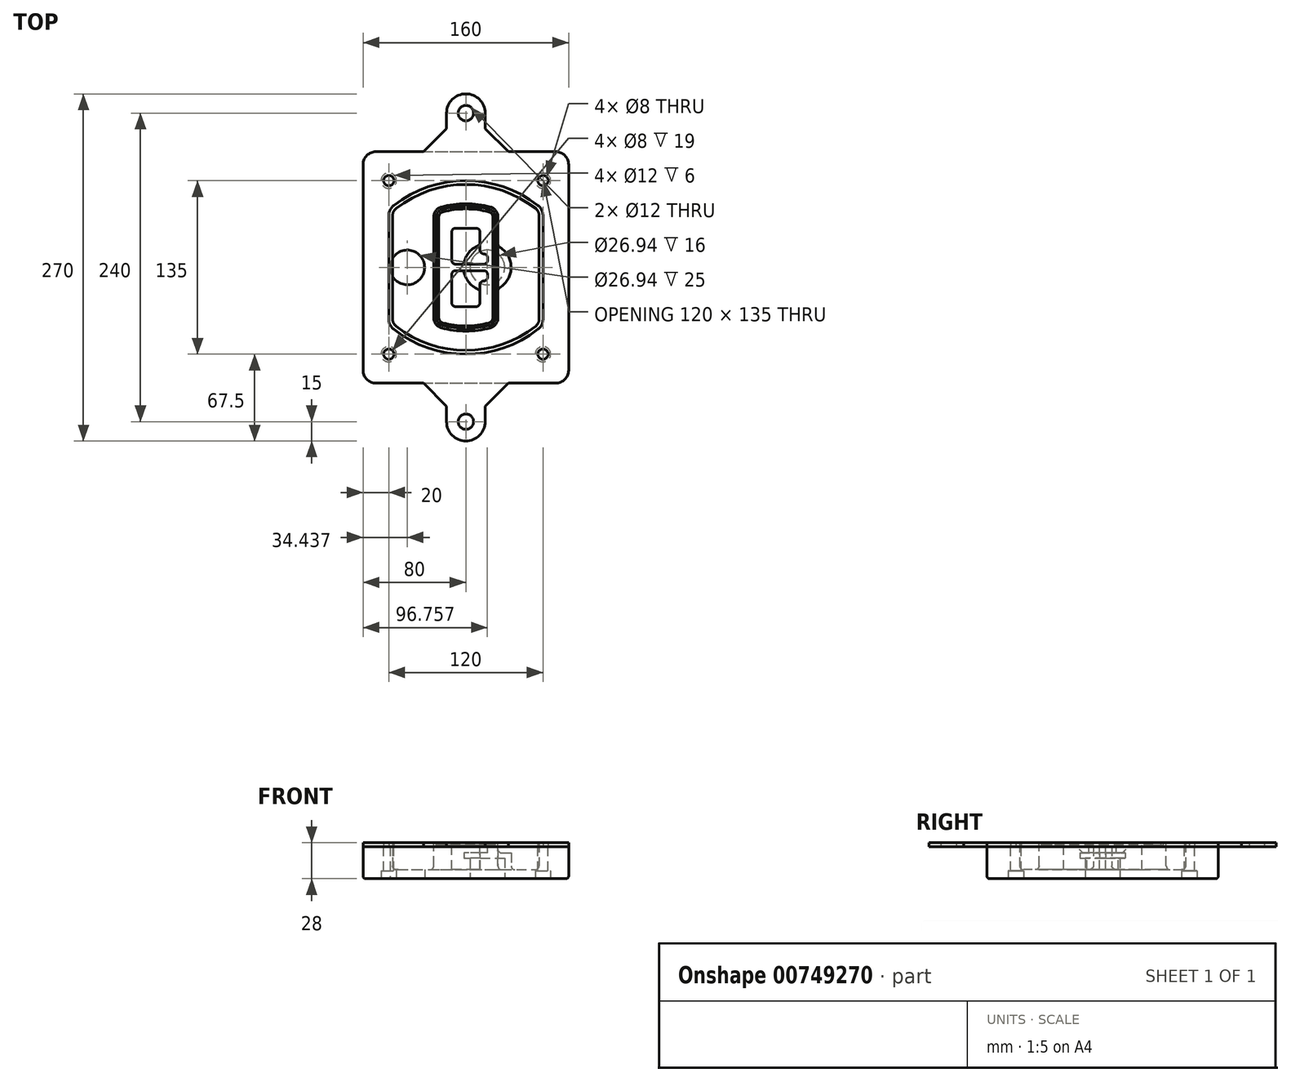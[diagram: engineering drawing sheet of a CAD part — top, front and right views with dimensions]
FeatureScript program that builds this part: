
annotation { "Feature Type Name" : "Feature", "Feature Type Description" : "" }
export const myFeature = defineFeature(function(context is Context, id is Id, definition is map)
    precondition{}
    {
        {
            var Q0;
            Q0=qCreatedBy(makeId("Top.planeOp"),FACE);
            var sketch = newSketch(context, id + "F0", { "sketchPlane" : qUnion([Q0])});
            skPoint(sketch, "E0.rect.middle", {"position": v(0, 0) * mm});
            skLineSegment(sketch, "E1.bottom", {"start": v(-70, -90) * mm, "end": v(70, -90) * mm});
            skLineSegment(sketch, "E1.top", {"start": v(-70, 90) * mm, "end": v(70, 90) * mm});
            skLineSegment(sketch, "E1.left", {"start": v(-80, -80) * mm, "end": v(-80, 80) * mm});
            skLineSegment(sketch, "E1.right", {"start": v(80, -80) * mm, "end": v(80, 80) * mm});
            skLineSegment(sketch, "E2", {"start": v(-80, 90) * mm, "end": v(80, -90) * mm, "construction": true});
            skLineSegment(sketch, "E3", {"start": v(80, 90) * mm, "end": v(-80, -90) * mm, "construction": true});
            skCircle(sketch, "E4", {"center": v(-60, 67.5) * mm, "radius": 4 * mm});
            skCircle(sketch, "E5", {"center": v(60, 67.5) * mm, "radius": 4 * mm});
            skCircle(sketch, "E6", {"center": v(60, -67.5) * mm, "radius": 4 * mm});
            skCircle(sketch, "E7", {"center": v(-60, -67.5) * mm, "radius": 4 * mm});
            skLineSegment(sketch, "E8", {"start": v(-60, 67.5) * mm, "end": v(60, 67.5) * mm, "construction": true});
            skLineSegment(sketch, "E9", {"start": v(60, 67.5) * mm, "end": v(60, -67.5) * mm, "construction": true});
            skLineSegment(sketch, "E10", {"start": v(60, -67.5) * mm, "end": v(-60, -67.5) * mm, "construction": true});
            skLineSegment(sketch, "E11", {"start": v(-60, -67.5) * mm, "end": v(-60, 67.5) * mm, "construction": true});
            skLineSegment(sketch, "E12", {"start": v(-60, 40.3) * mm, "end": v(-60, -40.3) * mm});
            skLineSegment(sketch, "E13", {"start": v(60, 40.3) * mm, "end": v(60, -40.3) * mm});
            skArc(sketch, "E14", {"start": v(56.15, 48.18) * mm, "mid": v(0, 67.5) * mm, "end": v(-56.15, 48.18) * mm});
            skArc(sketch, "E15", {"start": v(-56.15, -48.18) * mm, "mid": v(0, -67.5) * mm, "end": v(56.15, -48.18) * mm});
            skLineSegment(sketch, "E16", {"start": v(-60, 0) * mm, "end": v(60, 0) * mm, "construction": true});
            skPoint(sketch, "E17.visualSharp", {"position": v(-60, -45) * mm});
            skArc(sketch, "E17.filletArc", {"start": v(-60, -40.3) * mm, "mid": v(-58.99, -44.68) * mm, "end": v(-56.15, -48.18) * mm});
            skPoint(sketch, "E18.visualSharp", {"position": v(-60, 45) * mm});
            skArc(sketch, "E18.filletArc", {"start": v(-56.15, 48.18) * mm, "mid": v(-58.99, 44.68) * mm, "end": v(-60, 40.3) * mm});
            skPoint(sketch, "E19.visualSharp", {"position": v(60, 45) * mm});
            skArc(sketch, "E19.filletArc", {"start": v(60, 40.3) * mm, "mid": v(58.99, 44.68) * mm, "end": v(56.15, 48.18) * mm});
            skPoint(sketch, "E20.visualSharp", {"position": v(60, -45) * mm});
            skArc(sketch, "E20.filletArc", {"start": v(56.15, -48.18) * mm, "mid": v(58.99, -44.68) * mm, "end": v(60, -40.3) * mm});
            skPoint(sketch, "E21.visualSharp", {"position": v(-80, 90) * mm});
            skArc(sketch, "E21.filletArc", {"start": v(-70, 90) * mm, "mid": v(-77.07, 87.07) * mm, "end": v(-80, 80) * mm});
            skPoint(sketch, "E22.visualSharp", {"position": v(80, 90) * mm});
            skArc(sketch, "E22.filletArc", {"start": v(80, 80) * mm, "mid": v(77.07, 87.07) * mm, "end": v(70, 90) * mm});
            skPoint(sketch, "E23.visualSharp", {"position": v(80, -90) * mm});
            skArc(sketch, "E23.filletArc", {"start": v(70, -90) * mm, "mid": v(77.07, -87.07) * mm, "end": v(80, -80) * mm});
            skPoint(sketch, "E24.visualSharp", {"position": v(-80, -90) * mm});
            skArc(sketch, "E24.filletArc", {"start": v(-80, -80) * mm, "mid": v(-77.07, -87.07) * mm, "end": v(-70, -90) * mm});
            skArc(sketch, "E25.0", {"start": v(57, 40.3) * mm, "mid": v(56.3, 43.36) * mm, "end": v(54.3, 45.81) * mm});
            skLineSegment(sketch, "E25.1", {"start": v(57, 40.3) * mm, "end": v(57, -40.3) * mm});
            skArc(sketch, "E25.2", {"start": v(54.3, -45.81) * mm, "mid": v(56.3, -43.36) * mm, "end": v(57, -40.3) * mm});
            skArc(sketch, "E25.3", {"start": v(-54.3, -45.81) * mm, "mid": v(0, -64.5) * mm, "end": v(54.3, -45.81) * mm});
            skArc(sketch, "E25.4", {"start": v(-57, -40.3) * mm, "mid": v(-56.3, -43.36) * mm, "end": v(-54.3, -45.81) * mm});
            skArc(sketch, "E25.5", {"start": v(54.3, 45.81) * mm, "mid": v(0, 64.5) * mm, "end": v(-54.3, 45.81) * mm});
            skLineSegment(sketch, "E25.6", {"start": v(-57, 40.3) * mm, "end": v(-57, -40.3) * mm});
            skArc(sketch, "E25.7", {"start": v(-54.3, 45.81) * mm, "mid": v(-56.3, 43.36) * mm, "end": v(-57, 40.3) * mm});
            skArc(sketch, "E26.0", {"start": v(-58.62, 51.33) * mm, "mid": v(-62.58, 46.43) * mm, "end": v(-64, 40.3) * mm});
            skArc(sketch, "E26.1", {"start": v(58.62, 51.33) * mm, "mid": v(0, 71.5) * mm, "end": v(-58.62, 51.33) * mm});
            skArc(sketch, "E26.2", {"start": v(64, 40.3) * mm, "mid": v(62.58, 46.43) * mm, "end": v(58.62, 51.33) * mm});
            skLineSegment(sketch, "E26.3", {"start": v(64, 40.3) * mm, "end": v(64, -40.3) * mm});
            skArc(sketch, "E26.4", {"start": v(58.62, -51.33) * mm, "mid": v(62.58, -46.43) * mm, "end": v(64, -40.3) * mm});
            skLineSegment(sketch, "E26.5", {"start": v(-64, 40.3) * mm, "end": v(-64, -40.3) * mm});
            skArc(sketch, "E26.6", {"start": v(-58.62, -51.33) * mm, "mid": v(0, -71.5) * mm, "end": v(58.62, -51.33) * mm});
            skArc(sketch, "E26.7", {"start": v(-64, -40.3) * mm, "mid": v(-62.58, -46.43) * mm, "end": v(-58.62, -51.33) * mm});
            skSolve(sketch);
        }
        {
            var Q0;
            Q0=makeQuery(id+"F0.imprint","IMPRINT",FACE,{"disambiguationData":[TD([[makeQuery(id+"F0.imprint","IMPRINT",EDGE,{"derivedFrom":sQuery(id+"F0.wireOp",EDGE,"E1.bottom")}),1.0]])]});
            var Q1;
            Q1=makeQuery(id+"F0.imprint","IMPRINT",FACE,{"disambiguationData":[TD([[makeQuery(id+"F0.imprint","IMPRINT",EDGE,{"derivedFrom":sQuery(id+"F0.wireOp",EDGE,"E12")}),1.0]])]});
            var Q2;
            Q2=makeQuery(id+"F0.imprint","IMPRINT",FACE,{"disambiguationData":[TD([[makeQuery(id+"F0.imprint","IMPRINT",EDGE,{"derivedFrom":sQuery(id+"F0.wireOp",EDGE,"E25.0")}),1.0]])]});
            var Q3;
            Q3=makeQuery(id+"F0.imprint","IMPRINT",FACE,{"disambiguationData":[TD([[makeQuery(id+"F0.imprint","IMPRINT",EDGE,{"derivedFrom":sQuery(id+"F0.wireOp",EDGE,"E12")}),-1.0]])]});
            extrude(context, id + "F1", {"entities" : qUnion([Q0, Q1, Q2, Q3]), "oppositeDirection" : true, "depth" : 25 * mm});
        }
        {
            var Q0;
            Q0=makeQuery(id+"F0.imprint","IMPRINT",FACE,{"disambiguationData":[TD([[makeQuery(id+"F0.imprint","IMPRINT",EDGE,{"derivedFrom":sQuery(id+"F0.wireOp",EDGE,"E12")}),1.0]])]});
            extrude(context, id + "F2", {"entities" : qUnion([Q0]), "operationType" : NewBodyOperationType.ADD, "depth" : 3 * mm});
        }
        {
            var Q0;
            Q0=makeQuery(id+"F0.imprint","IMPRINT",FACE,{"disambiguationData":[TD([[makeQuery(id+"F0.imprint","IMPRINT",EDGE,{"derivedFrom":sQuery(id+"F0.wireOp",EDGE,"E25.0")}),1.0]])]});
            extrude(context, id + "F3", {"entities" : qUnion([Q0]), "operationType" : NewBodyOperationType.REMOVE, "oppositeDirection" : true, "depth" : 18 * mm});
        }
        {
            var Q0;
            Q0=makeQuery(id+"F2.opExtrude","CAP_FACE",FACE,{"disambiguationData":[OSD([sQuery(id+"F0.wireOp",EDGE,"E12"),sQuery(id+"F0.wireOp",EDGE,"E13"),sQuery(id+"F0.wireOp",EDGE,"E14"),sQuery(id+"F0.wireOp",EDGE,"E15"),sQuery(id+"F0.wireOp",EDGE,"E17.filletArc"),sQuery(id+"F0.wireOp",EDGE,"E18.filletArc"),sQuery(id+"F0.wireOp",EDGE,"E19.filletArc"),sQuery(id+"F0.wireOp",EDGE,"E20.filletArc"),sQuery(id+"F0.wireOp",EDGE,"E25.0"),sQuery(id+"F0.wireOp",EDGE,"E25.1"),sQuery(id+"F0.wireOp",EDGE,"E25.2"),sQuery(id+"F0.wireOp",EDGE,"E25.3"),sQuery(id+"F0.wireOp",EDGE,"E25.4"),sQuery(id+"F0.wireOp",EDGE,"E25.5"),sQuery(id+"F0.wireOp",EDGE,"E25.6"),sQuery(id+"F0.wireOp",EDGE,"E25.7")])],"isStart":false});
            var sketch = newSketch(context, id + "F4", { "sketchPlane" : qUnion([Q0])});
            skArc(sketch, "E27.0", {"start": v(-19.08, -46.97) * mm, "mid": v(0, -49.5) * mm, "end": v(19.08, -46.97) * mm});
            skArc(sketch, "E28.0", {"start": v(19.08, 46.97) * mm, "mid": v(0, 49.5) * mm, "end": v(-19.08, 46.97) * mm});
            skLineSegment(sketch, "E29", {"start": v(-25, 39.25) * mm, "end": v(-25, -39.25) * mm});
            skLineSegment(sketch, "E30", {"start": v(25, 39.25) * mm, "end": v(25, -39.25) * mm});
            skLineSegment(sketch, "E31", {"start": v(-25, 45.1) * mm, "end": v(25, 45.1) * mm, "construction": true});
            skLineSegment(sketch, "E32", {"start": v(-25, -45.1) * mm, "end": v(25, -45.1) * mm, "construction": true});
            skPoint(sketch, "E33.visualSharp", {"position": v(-25, 45.1) * mm});
            skArc(sketch, "E33.filletArc", {"start": v(-19.08, 46.97) * mm, "mid": v(-23.35, 44.11) * mm, "end": v(-25, 39.25) * mm});
            skPoint(sketch, "E34.visualSharp", {"position": v(25, 45.1) * mm});
            skArc(sketch, "E34.filletArc", {"start": v(25, 39.25) * mm, "mid": v(23.35, 44.11) * mm, "end": v(19.08, 46.97) * mm});
            skPoint(sketch, "E35.visualSharp", {"position": v(25, -45.1) * mm});
            skArc(sketch, "E35.filletArc", {"start": v(19.08, -46.97) * mm, "mid": v(23.35, -44.11) * mm, "end": v(25, -39.25) * mm});
            skPoint(sketch, "E36.visualSharp", {"position": v(-25, -45.1) * mm});
            skArc(sketch, "E36.filletArc", {"start": v(-25, -39.25) * mm, "mid": v(-23.35, -44.11) * mm, "end": v(-19.08, -46.97) * mm});
            skArc(sketch, "E37.0", {"start": v(54.3, 45.81) * mm, "mid": v(0, 64.5) * mm, "end": v(-54.3, 45.81) * mm});
            skArc(sketch, "E37.1", {"start": v(-54.3, 45.81) * mm, "mid": v(-56.3, 43.36) * mm, "end": v(-57, 40.3) * mm});
            skLineSegment(sketch, "E37.2", {"start": v(-57, 40.3) * mm, "end": v(-57, -40.3) * mm});
            skArc(sketch, "E37.3", {"start": v(-57, -40.3) * mm, "mid": v(-56.3, -43.36) * mm, "end": v(-54.3, -45.81) * mm});
            skArc(sketch, "E37.4", {"start": v(-54.3, -45.81) * mm, "mid": v(0, -64.5) * mm, "end": v(54.3, -45.81) * mm});
            skArc(sketch, "E37.5", {"start": v(54.3, -45.81) * mm, "mid": v(56.3, -43.36) * mm, "end": v(57, -40.3) * mm});
            skLineSegment(sketch, "E37.6", {"start": v(57, 40.3) * mm, "end": v(57, -40.3) * mm});
            skArc(sketch, "E37.7", {"start": v(57, 40.3) * mm, "mid": v(56.3, 43.36) * mm, "end": v(54.3, 45.81) * mm});
            skLineSegment(sketch, "E38.0", {"start": v(23, 39.25) * mm, "end": v(23, -39.25) * mm});
            skArc(sketch, "E38.1", {"start": v(18.56, -45.04) * mm, "mid": v(21.76, -42.9) * mm, "end": v(23, -39.25) * mm});
            skArc(sketch, "E38.2", {"start": v(-18.56, -45.04) * mm, "mid": v(0, -47.5) * mm, "end": v(18.56, -45.04) * mm});
            skArc(sketch, "E38.3", {"start": v(-23, -39.25) * mm, "mid": v(-21.76, -42.9) * mm, "end": v(-18.56, -45.04) * mm});
            skLineSegment(sketch, "E38.4", {"start": v(-23, 39.25) * mm, "end": v(-23, -39.25) * mm});
            skArc(sketch, "E38.5", {"start": v(23, 39.25) * mm, "mid": v(21.76, 42.9) * mm, "end": v(18.56, 45.04) * mm});
            skArc(sketch, "E38.6", {"start": v(-18.56, 45.04) * mm, "mid": v(-21.76, 42.9) * mm, "end": v(-23, 39.25) * mm});
            skArc(sketch, "E38.7", {"start": v(18.56, 45.04) * mm, "mid": v(0, 47.5) * mm, "end": v(-18.56, 45.04) * mm});
            skArc(sketch, "E39.0", {"start": v(21, 39.25) * mm, "mid": v(20.18, 41.68) * mm, "end": v(18.04, 43.1) * mm});
            skLineSegment(sketch, "E39.1", {"start": v(21, 39.25) * mm, "end": v(21, -39.25) * mm});
            skArc(sketch, "E39.2", {"start": v(18.04, -43.1) * mm, "mid": v(20.18, -41.68) * mm, "end": v(21, -39.25) * mm});
            skArc(sketch, "E39.3", {"start": v(-18.04, -43.1) * mm, "mid": v(0, -45.5) * mm, "end": v(18.04, -43.1) * mm});
            skArc(sketch, "E39.4", {"start": v(-21, -39.25) * mm, "mid": v(-20.18, -41.68) * mm, "end": v(-18.04, -43.1) * mm});
            skArc(sketch, "E39.5", {"start": v(18.04, 43.1) * mm, "mid": v(0, 45.5) * mm, "end": v(-18.04, 43.1) * mm});
            skLineSegment(sketch, "E39.6", {"start": v(-21, 39.25) * mm, "end": v(-21, -39.25) * mm});
            skArc(sketch, "E39.7", {"start": v(-18.04, 43.1) * mm, "mid": v(-20.18, 41.68) * mm, "end": v(-21, 39.25) * mm});
            skLineSegment(sketch, "E40", {"start": v(-25, 0) * mm, "end": v(25, 0) * mm, "construction": true});
            skLineSegment(sketch, "E41", {"start": v(-11, 5.5) * mm, "end": v(-11, 27.5) * mm});
            skLineSegment(sketch, "E42", {"start": v(-8, 30.5) * mm, "end": v(8, 30.5) * mm});
            skLineSegment(sketch, "E43", {"start": v(11, 27.5) * mm, "end": v(11, 13.5) * mm});
            skLineSegment(sketch, "E44", {"start": v(14, 10.5) * mm, "end": v(14, 10.5) * mm});
            skLineSegment(sketch, "E45", {"start": v(17, 7.5) * mm, "end": v(17, 5.5) * mm});
            skLineSegment(sketch, "E46", {"start": v(14, 2.5) * mm, "end": v(-8, 2.5) * mm});
            skPoint(sketch, "E47.visualSharp", {"position": v(-11, 30.5) * mm});
            skArc(sketch, "E47.filletArc", {"start": v(-8, 30.5) * mm, "mid": v(-10.12, 29.62) * mm, "end": v(-11, 27.5) * mm});
            skPoint(sketch, "E48.visualSharp", {"position": v(11, 30.5) * mm});
            skArc(sketch, "E48.filletArc", {"start": v(11, 27.5) * mm, "mid": v(10.12, 29.62) * mm, "end": v(8, 30.5) * mm});
            skPoint(sketch, "E49.visualSharp", {"position": v(11, 10.5) * mm});
            skArc(sketch, "E49.filletArc", {"start": v(11, 13.5) * mm, "mid": v(11.88, 11.38) * mm, "end": v(14, 10.5) * mm});
            skPoint(sketch, "E50.visualSharp", {"position": v(17, 10.5) * mm});
            skArc(sketch, "E50.filletArc", {"start": v(17, 7.5) * mm, "mid": v(16.12, 9.62) * mm, "end": v(14, 10.5) * mm});
            skPoint(sketch, "E51.visualSharp", {"position": v(17, 2.5) * mm});
            skArc(sketch, "E51.filletArc", {"start": v(14, 2.5) * mm, "mid": v(16.12, 3.38) * mm, "end": v(17, 5.5) * mm});
            skPoint(sketch, "E52.visualSharp", {"position": v(-11, 2.5) * mm});
            skArc(sketch, "E52.filletArc", {"start": v(-11, 5.5) * mm, "mid": v(-10.12, 3.38) * mm, "end": v(-8, 2.5) * mm});
            skLineSegment(sketch, "E53.0.MirrorCS", {"start": v(14, -2.5) * mm, "end": v(-8, -2.5) * mm});
            skArc(sketch, "E54.0.MirrorCS", {"start": v(-11, -5.5) * mm, "mid": v(-10.12, -3.38) * mm, "end": v(-8, -2.5) * mm});
            skLineSegment(sketch, "E55.0.MirrorCS", {"start": v(-11, -5.5) * mm, "end": v(-11, -27.5) * mm});
            skArc(sketch, "E56.0.MirrorCS", {"start": v(-8, -30.5) * mm, "mid": v(-10.12, -29.62) * mm, "end": v(-11, -27.5) * mm});
            skLineSegment(sketch, "E57.0.MirrorCS", {"start": v(-8, -30.5) * mm, "end": v(8, -30.5) * mm});
            skArc(sketch, "E58.0.MirrorCS", {"start": v(11, -27.5) * mm, "mid": v(10.12, -29.62) * mm, "end": v(8, -30.5) * mm});
            skLineSegment(sketch, "E59.0.MirrorCS", {"start": v(11, -27.5) * mm, "end": v(11, -13.5) * mm});
            skArc(sketch, "E60.0.MirrorCS", {"start": v(11, -13.5) * mm, "mid": v(11.88, -11.38) * mm, "end": v(14, -10.5) * mm});
            skArc(sketch, "E61.0.MirrorCS", {"start": v(17, -7.5) * mm, "mid": v(16.12, -9.62) * mm, "end": v(14, -10.5) * mm});
            skLineSegment(sketch, "E62.0.MirrorCS", {"start": v(17, -7.5) * mm, "end": v(17, -5.5) * mm});
            skArc(sketch, "E63.0.MirrorCS", {"start": v(14, -2.5) * mm, "mid": v(16.12, -3.38) * mm, "end": v(17, -5.5) * mm});
            skSolve(sketch);
        }
        {
            var Q0;
            Q0=makeQuery(id+"F4.imprint","IMPRINT",FACE,{"disambiguationData":[TD([[makeQuery(id+"F4.imprint","IMPRINT",EDGE,{"derivedFrom":sQuery(id+"F4.wireOp",EDGE,"E27.0")}),1.0]])]});
            var Q1;
            Q1=makeQuery(id+"F4.imprint","IMPRINT",FACE,{"disambiguationData":[TD([[makeQuery(id+"F4.imprint","IMPRINT",EDGE,{"derivedFrom":sQuery(id+"F4.wireOp",EDGE,"E38.0")}),-1.0]])]});
            var Q2;
            Q2=makeQuery(id+"F4.imprint","IMPRINT",FACE,{"disambiguationData":[TD([[makeQuery(id+"F4.imprint","IMPRINT",EDGE,{"derivedFrom":sQuery(id+"F4.wireOp",EDGE,"E39.0")}),1.0]])]});
            extrude(context, id + "F5", {"entities" : qUnion([Q0, Q1, Q2]), "operationType" : NewBodyOperationType.ADD, "endBound" : BoundingType.UP_TO_NEXT, "oppositeDirection" : true, "depth" : 25 * mm});
        }
        {
            var Q0;
            Q0=makeQuery(id+"F4.imprint","IMPRINT",FACE,{"disambiguationData":[TD([[makeQuery(id+"F4.imprint","IMPRINT",EDGE,{"derivedFrom":sQuery(id+"F4.wireOp",EDGE,"E38.0")}),-1.0]])]});
            extrude(context, id + "F6", {"entities" : qUnion([Q0]), "operationType" : NewBodyOperationType.REMOVE, "oppositeDirection" : true, "depth" : 2 * mm});
        }
        {
            var Q0;
            Q0=makeQuery(id+"F1.opExtrude","CAP_FACE",FACE,{"disambiguationData":[OSD([sQuery(id+"F0.wireOp",EDGE,"E1.bottom"),sQuery(id+"F0.wireOp",EDGE,"E1.top"),sQuery(id+"F0.wireOp",EDGE,"E1.left"),sQuery(id+"F0.wireOp",EDGE,"E1.right"),sQuery(id+"F0.wireOp",EDGE,"E4"),sQuery(id+"F0.wireOp",EDGE,"E5"),sQuery(id+"F0.wireOp",EDGE,"E6"),sQuery(id+"F0.wireOp",EDGE,"E7"),sQuery(id+"F0.wireOp",EDGE,"E21.filletArc"),sQuery(id+"F0.wireOp",EDGE,"E22.filletArc"),sQuery(id+"F0.wireOp",EDGE,"E23.filletArc"),sQuery(id+"F0.wireOp",EDGE,"E24.filletArc")])],"isStart":false});
            var sketch = newSketch(context, id + "F7", { "sketchPlane" : qUnion([Q0])});
            skCircle(sketch, "E64", {"center": v(16.76, 0) * mm, "radius": 13.47 * mm});
            skCircle(sketch, "E65", {"center": v(-45.56, 0) * mm, "radius": 13.47 * mm});
            skLineSegment(sketch, "E66", {"start": v(80, 0) * mm, "end": v(-80, 0) * mm});
            skCircle(sketch, "E67", {"center": v(16.76, 0) * mm, "radius": 18.47 * mm});
            skCircle(sketch, "E68", {"center": v(60, -67.5) * mm, "radius": 6 * mm});
            skCircle(sketch, "E69", {"center": v(-60, -67.5) * mm, "radius": 6 * mm});
            skCircle(sketch, "E70", {"center": v(-60, 67.5) * mm, "radius": 6 * mm});
            skCircle(sketch, "E71", {"center": v(60, 67.5) * mm, "radius": 6 * mm});
            skSolve(sketch);
        }
        {
            var Q0;
            {var subQ1=sQuery(id+"F7.wireOp",EDGE,"E66");var subQ4=sQuery(id+"F7.wireOp",EDGE,"E64");var subQ6=makeQuery(id+"F7.imprint","INTERSECT",VERTEX,{"disambiguationData":[OD(0.0)],"derivedFrom":[subQ4,subQ1]});Q0=makeQuery(id+"F7.imprint","IMPRINT",FACE,{"disambiguationData":[TD([[makeQuery(id+"F7.imprint","IMPRINT",EDGE,{"disambiguationData":[TD([[subQ6,-1.0]])],"derivedFrom":subQ4}),-1.0]])]});}
            var Q1;
            {var subQ0=sQuery(id+"F7.wireOp",EDGE,"E66");var subQ1=sQuery(id+"F7.wireOp",EDGE,"E64");var subQ3=makeQuery(id+"F7.imprint","INTERSECT",VERTEX,{"disambiguationData":[OD(0.0)],"derivedFrom":[subQ1,subQ0]});Q1=makeQuery(id+"F7.imprint","IMPRINT",FACE,{"disambiguationData":[TD([[makeQuery(id+"F7.imprint","IMPRINT",EDGE,{"disambiguationData":[TD([[subQ3,-1.0]])],"derivedFrom":subQ1}),1.0]])]});}
            var Q2;
            {var subQ0=sQuery(id+"F7.wireOp",EDGE,"E66");var subQ1=sQuery(id+"F7.wireOp",EDGE,"E64");var subQ3=makeQuery(id+"F7.imprint","INTERSECT",VERTEX,{"disambiguationData":[OD(0.0)],"derivedFrom":[subQ1,subQ0]});Q2=makeQuery(id+"F7.imprint","IMPRINT",FACE,{"disambiguationData":[TD([[makeQuery(id+"F7.imprint","IMPRINT",EDGE,{"disambiguationData":[TD([[subQ3,1.0]])],"derivedFrom":subQ1}),1.0]])]});}
            var Q3;
            {var subQ1=sQuery(id+"F7.wireOp",EDGE,"E66");var subQ4=sQuery(id+"F7.wireOp",EDGE,"E64");var subQ6=makeQuery(id+"F7.imprint","INTERSECT",VERTEX,{"disambiguationData":[OD(0.0)],"derivedFrom":[subQ4,subQ1]});Q3=makeQuery(id+"F7.imprint","IMPRINT",FACE,{"disambiguationData":[TD([[makeQuery(id+"F7.imprint","IMPRINT",EDGE,{"disambiguationData":[TD([[subQ6,1.0]])],"derivedFrom":subQ4}),-1.0]])]});}
            extrude(context, id + "F8", {"entities" : qUnion([Q0, Q1, Q2, Q3]), "operationType" : NewBodyOperationType.ADD, "oppositeDirection" : true, "depth" : 20 * mm});
        }
        {
            var Q0;
            {var subQ0=sQuery(id+"F7.wireOp",EDGE,"E66");var subQ1=sQuery(id+"F7.wireOp",EDGE,"E64");var subQ3=makeQuery(id+"F7.imprint","INTERSECT",VERTEX,{"disambiguationData":[OD(0.0)],"derivedFrom":[subQ1,subQ0]});Q0=makeQuery(id+"F7.imprint","IMPRINT",FACE,{"disambiguationData":[TD([[makeQuery(id+"F7.imprint","IMPRINT",EDGE,{"disambiguationData":[TD([[subQ3,-1.0]])],"derivedFrom":subQ1}),1.0]])]});}
            var Q1;
            {var subQ0=sQuery(id+"F7.wireOp",EDGE,"E66");var subQ1=sQuery(id+"F7.wireOp",EDGE,"E64");var subQ3=makeQuery(id+"F7.imprint","INTERSECT",VERTEX,{"disambiguationData":[OD(0.0)],"derivedFrom":[subQ1,subQ0]});Q1=makeQuery(id+"F7.imprint","IMPRINT",FACE,{"disambiguationData":[TD([[makeQuery(id+"F7.imprint","IMPRINT",EDGE,{"disambiguationData":[TD([[subQ3,1.0]])],"derivedFrom":subQ1}),1.0]])]});}
            extrude(context, id + "F9", {"entities" : qUnion([Q0, Q1]), "operationType" : NewBodyOperationType.REMOVE, "oppositeDirection" : true, "depth" : 16 * mm});
        }
        {
            var Q0;
            {var subQ0=sQuery(id+"F7.wireOp",EDGE,"E66");var subQ1=sQuery(id+"F7.wireOp",EDGE,"E65");var subQ3=makeQuery(id+"F7.imprint","INTERSECT",VERTEX,{"disambiguationData":[OD(0.0)],"derivedFrom":[subQ1,subQ0]});Q0=makeQuery(id+"F7.imprint","IMPRINT",FACE,{"disambiguationData":[TD([[makeQuery(id+"F7.imprint","IMPRINT",EDGE,{"disambiguationData":[TD([[subQ3,-1.0]])],"derivedFrom":subQ1}),1.0]])]});}
            var Q1;
            {var subQ0=sQuery(id+"F7.wireOp",EDGE,"E66");var subQ1=sQuery(id+"F7.wireOp",EDGE,"E65");var subQ3=makeQuery(id+"F7.imprint","INTERSECT",VERTEX,{"disambiguationData":[OD(0.0)],"derivedFrom":[subQ1,subQ0]});Q1=makeQuery(id+"F7.imprint","IMPRINT",FACE,{"disambiguationData":[TD([[makeQuery(id+"F7.imprint","IMPRINT",EDGE,{"disambiguationData":[TD([[subQ3,1.0]])],"derivedFrom":subQ1}),1.0]])]});}
            extrude(context, id + "F10", {"entities" : qUnion([Q0, Q1]), "operationType" : NewBodyOperationType.REMOVE, "oppositeDirection" : true, "depth" : 25 * mm});
        }
        {
            var Q0;
            Q0=makeQuery(id+"F7.imprint","IMPRINT",FACE,{"disambiguationData":[TD([[makeQuery(id+"F7.imprint","IMPRINT",EDGE,{"derivedFrom":sQuery(id+"F7.wireOp",EDGE,"E68")}),1.0]])]});
            var Q1;
            Q1=makeQuery(id+"F7.imprint","IMPRINT",FACE,{"disambiguationData":[TD([[makeQuery(id+"F7.imprint","IMPRINT",EDGE,{"derivedFrom":makeQuery(id+"F1.opExtrude","CAP_EDGE",EDGE,{"disambiguationData":[OSD([sQuery(id+"F0.wireOp",EDGE,"E5")])],"isStart":false})}),-1.0]])]});
            var Q2;
            Q2=makeQuery(id+"F7.imprint","IMPRINT",FACE,{"disambiguationData":[TD([[makeQuery(id+"F7.imprint","IMPRINT",EDGE,{"derivedFrom":sQuery(id+"F7.wireOp",EDGE,"E69")}),1.0]])]});
            var Q3;
            Q3=makeQuery(id+"F7.imprint","IMPRINT",FACE,{"disambiguationData":[TD([[makeQuery(id+"F7.imprint","IMPRINT",EDGE,{"derivedFrom":makeQuery(id+"F1.opExtrude","CAP_EDGE",EDGE,{"disambiguationData":[OSD([sQuery(id+"F0.wireOp",EDGE,"E4")])],"isStart":false})}),-1.0]])]});
            var Q4;
            Q4=makeQuery(id+"F7.imprint","IMPRINT",FACE,{"disambiguationData":[TD([[makeQuery(id+"F7.imprint","IMPRINT",EDGE,{"derivedFrom":sQuery(id+"F7.wireOp",EDGE,"E70")}),1.0]])]});
            var Q5;
            Q5=makeQuery(id+"F7.imprint","IMPRINT",FACE,{"disambiguationData":[TD([[makeQuery(id+"F7.imprint","IMPRINT",EDGE,{"derivedFrom":makeQuery(id+"F1.opExtrude","CAP_EDGE",EDGE,{"disambiguationData":[OSD([sQuery(id+"F0.wireOp",EDGE,"E7")])],"isStart":false})}),-1.0]])]});
            var Q6;
            Q6=makeQuery(id+"F7.imprint","IMPRINT",FACE,{"disambiguationData":[TD([[makeQuery(id+"F7.imprint","IMPRINT",EDGE,{"derivedFrom":sQuery(id+"F7.wireOp",EDGE,"E71")}),1.0]])]});
            var Q7;
            Q7=makeQuery(id+"F7.imprint","IMPRINT",FACE,{"disambiguationData":[TD([[makeQuery(id+"F7.imprint","IMPRINT",EDGE,{"derivedFrom":makeQuery(id+"F1.opExtrude","CAP_EDGE",EDGE,{"disambiguationData":[OSD([sQuery(id+"F0.wireOp",EDGE,"E6")])],"isStart":false})}),-1.0]])]});
            extrude(context, id + "F11", {"entities" : qUnion([Q0, Q1, Q2, Q3, Q4, Q5, Q6, Q7]), "operationType" : NewBodyOperationType.REMOVE, "oppositeDirection" : true, "depth" : 6 * mm});
        }
        {
            var Q0;
            Q0=makeQuery(id+"F9.boolean.opBoolean","COPY",FACE,{"derivedFrom":makeQuery(id+"F9.opExtrude","CAP_FACE",FACE,{"disambiguationData":[OSD([sQuery(id+"F7.wireOp",EDGE,"E64")])],"isStart":false})});
            var sketch = newSketch(context, id + "F12", { "sketchPlane" : qUnion([Q0])});
            skArc(sketch, "E72.0", {"start": v(11, 17.55) * mm, "mid": v(2.57, 11.82) * mm, "end": v(-1.54, 2.5) * mm});
            skArc(sketch, "E72.1", {"start": v(-1.54, -2.5) * mm, "mid": v(2.57, -11.82) * mm, "end": v(11, -17.55) * mm});
            skLineSegment(sketch, "E73", {"start": v(-1.54, -2.5) * mm, "end": v(14, -2.5) * mm});
            skLineSegment(sketch, "E74.0", {"start": v(14, 2.5) * mm, "end": v(-1.54, 2.5) * mm});
            skArc(sketch, "E74.1", {"start": v(14, 2.5) * mm, "mid": v(16.12, 3.38) * mm, "end": v(17, 5.5) * mm});
            skLineSegment(sketch, "E74.2", {"start": v(17, 7.5) * mm, "end": v(17, 5.5) * mm});
            skArc(sketch, "E74.3", {"start": v(17, 7.5) * mm, "mid": v(16.12, 9.62) * mm, "end": v(14, 10.5) * mm});
            skArc(sketch, "E74.4", {"start": v(11, 13.5) * mm, "mid": v(11.88, 11.38) * mm, "end": v(14, 10.5) * mm});
            skLineSegment(sketch, "E74.5", {"start": v(11, 17.55) * mm, "end": v(11, 13.5) * mm});
            skLineSegment(sketch, "E74.7", {"start": v(14, -2.5) * mm, "end": v(-1.54, -2.5) * mm});
            skArc(sketch, "E74.8", {"start": v(14, -2.5) * mm, "mid": v(16.12, -3.38) * mm, "end": v(17, -5.5) * mm});
            skLineSegment(sketch, "E74.9", {"start": v(17, -7.5) * mm, "end": v(17, -5.5) * mm});
            skArc(sketch, "E74.10", {"start": v(17, -7.5) * mm, "mid": v(16.12, -9.62) * mm, "end": v(14, -10.5) * mm});
            skArc(sketch, "E74.11", {"start": v(11, -13.5) * mm, "mid": v(11.88, -11.38) * mm, "end": v(14, -10.5) * mm});
            skLineSegment(sketch, "E74.12", {"start": v(11, -17.55) * mm, "end": v(11, -13.5) * mm});
            skPoint(sketch, "E75.orphan", {"position": v(11, -27.5) * mm});
            skPoint(sketch, "E76.orphan", {"position": v(-8, -2.5) * mm});
            skPoint(sketch, "E77.orphan", {"position": v(-8, 2.5) * mm});
            skPoint(sketch, "E78.orphan", {"position": v(11, 27.5) * mm});
            skSolve(sketch);
        }
        {
            var Q0;
            {var subQ7=sQuery(id+"F12.wireOp",EDGE,"E72.0");var subQ14=sQuery(id+"F12.wireOp",EDGE,"E72.1");var subQ16=sQuery(id+"F12.wireOp",EDGE,"E74.1");var subQ18=sQuery(id+"F12.wireOp",EDGE,"E74.8");Q0=qUnion([makeQuery(id+"F12.imprint","IMPRINT",FACE,{"disambiguationData":[TD([[makeQuery(id+"F12.imprint","IMPRINT",EDGE,{"derivedFrom":subQ7}),1.0]])]}),makeQuery(id+"F12.imprint","IMPRINT",FACE,{"disambiguationData":[TD([[makeQuery(id+"F12.imprint","IMPRINT",EDGE,{"derivedFrom":subQ14}),1.0]])]}),makeQuery(id+"F12.imprint","IMPRINT",FACE,{"disambiguationData":[TD([[makeQuery(id+"F12.imprint","IMPRINT",EDGE,{"derivedFrom":subQ16}),1.0]])]}),makeQuery(id+"F12.imprint","IMPRINT",FACE,{"disambiguationData":[TD([[makeQuery(id+"F12.imprint","IMPRINT",EDGE,{"derivedFrom":subQ18}),-1.0]])]})]);}
            var Q1;
            Q1=makeQuery(id+"F5.boolean.opBoolean","SPLIT",FACE,{"disambiguationData":[TD([makeQuery(id+"F5.opExtrude","SWEPT_FACE",FACE,{"disambiguationData":[OSD([sQuery(id+"F4.wireOp",EDGE,"E41")])]})])],"derivedFrom":makeQuery(id+"F3.boolean.opBoolean","COPY",FACE,{"derivedFrom":makeQuery(id+"F3.opExtrude","CAP_FACE",FACE,{"disambiguationData":[OSD([sQuery(id+"F0.wireOp",EDGE,"E25.0"),sQuery(id+"F0.wireOp",EDGE,"E25.1"),sQuery(id+"F0.wireOp",EDGE,"E25.2"),sQuery(id+"F0.wireOp",EDGE,"E25.3"),sQuery(id+"F0.wireOp",EDGE,"E25.4"),sQuery(id+"F0.wireOp",EDGE,"E25.5"),sQuery(id+"F0.wireOp",EDGE,"E25.6"),sQuery(id+"F0.wireOp",EDGE,"E25.7")])],"isStart":false})})});
            extrude(context, id + "F13", {"entities" : qUnion([Q0]), "operationType" : NewBodyOperationType.REMOVE, "endBound" : BoundingType.UP_TO_SURFACE, "endBoundEntityFace" : qUnion([Q1]), "depth" : 25 * mm});
        }
        {
            var Q0;
            Q0=makeQuery(id+"F3.boolean.opBoolean","COPY",EDGE,{"derivedFrom":makeQuery(id+"F3.opExtrude","CAP_EDGE",EDGE,{"disambiguationData":[OSD([sQuery(id+"F0.wireOp",EDGE,"E25.6")])],"isStart":false})});
            var Q1;
            Q1=makeQuery(id+"F8.boolean.opBoolean","INTERSECT",EDGE,{"derivedFrom":[makeQuery(id+"F5.opExtrude","SWEPT_FACE",FACE,{"disambiguationData":[OSD([sQuery(id+"F4.wireOp",EDGE,"E30")])]}),makeQuery(id+"F8.opExtrude","CAP_FACE",FACE,{"disambiguationData":[OSD([sQuery(id+"F7.wireOp",EDGE,"E67")])],"isStart":false})]});
            var Q2;
            Q2=makeQuery(id+"F8.boolean.opBoolean","INTERSECT",EDGE,{"disambiguationData":[OD(1.0)],"derivedFrom":[makeQuery(id+"F5.opExtrude","SWEPT_FACE",FACE,{"disambiguationData":[OSD([sQuery(id+"F4.wireOp",EDGE,"E30")])]}),makeQuery(id+"F8.opExtrude","SWEPT_FACE",FACE,{"disambiguationData":[OSD([sQuery(id+"F7.wireOp",EDGE,"E67")])]})]});
            var Q3;
            {var subQ0=sQuery(id+"F4.wireOp",EDGE,"E30");Q3=makeQuery(id+"F8.boolean.opBoolean","SPLIT",EDGE,{"disambiguationData":[TD([makeQuery(id+"F5.opExtrude","SWEPT_FACE",FACE,{"disambiguationData":[OSD([sQuery(id+"F4.wireOp",EDGE,"E35.filletArc")])]})])],"derivedFrom":makeQuery(id+"F5.opExtrude","CAP_EDGE",EDGE,{"disambiguationData":[OSD([subQ0])],"isStart":false})});}
            var Q4;
            {var subQ0=sQuery(id+"F0.wireOp",EDGE,"E25.7");var subQ1=sQuery(id+"F0.wireOp",EDGE,"E25.1");var subQ2=sQuery(id+"F0.wireOp",EDGE,"E25.6");var subQ3=sQuery(id+"F0.wireOp",EDGE,"E25.5");var subQ4=sQuery(id+"F0.wireOp",EDGE,"E25.4");var subQ5=sQuery(id+"F0.wireOp",EDGE,"E25.0");var subQ6=sQuery(id+"F0.wireOp",EDGE,"E25.2");var subQ7=sQuery(id+"F0.wireOp",EDGE,"E25.3");Q4=makeQuery(id+"F8.boolean.opBoolean","INTERSECT",EDGE,{"derivedFrom":[makeQuery(id+"F5.boolean.opBoolean","SPLIT",FACE,{"disambiguationData":[TD([makeQuery(id+"F2.opExtrude","SWEPT_FACE",FACE,{"disambiguationData":[OSD([subQ5])]})])],"derivedFrom":makeQuery(id+"F3.boolean.opBoolean","COPY",FACE,{"derivedFrom":makeQuery(id+"F3.opExtrude","CAP_FACE",FACE,{"disambiguationData":[OSD([subQ5,subQ1,subQ6,subQ7,subQ4,subQ3,subQ2,subQ0])],"isStart":false})})}),makeQuery(id+"F8.opExtrude","SWEPT_FACE",FACE,{"disambiguationData":[OSD([sQuery(id+"F7.wireOp",EDGE,"E67")])]})]});}
            var Q5;
            Q5=makeQuery(id+"F8.boolean.opBoolean","INTERSECT",EDGE,{"disambiguationData":[OD(0.0)],"derivedFrom":[makeQuery(id+"F5.opExtrude","SWEPT_FACE",FACE,{"disambiguationData":[OSD([sQuery(id+"F4.wireOp",EDGE,"E30")])]}),makeQuery(id+"F8.opExtrude","SWEPT_FACE",FACE,{"disambiguationData":[OSD([sQuery(id+"F7.wireOp",EDGE,"E67")])]})]});
            fillet(context, id + "F14", {"entities" : qUnion([Q0, Q1, Q2, Q3, Q4, Q5]), "radius" : 3 * mm, "tangentPropagation" : true, "allowEdgeOverflow" : false});
        }
        {
            var Q0;
            Q0=makeQuery(id+"F1.opExtrude","CAP_EDGE",EDGE,{"disambiguationData":[OSD([sQuery(id+"F0.wireOp",EDGE,"E1.bottom")])],"isStart":false});
            fillet(context, id + "F15", {"entities" : qUnion([Q0]), "radius" : 2 * mm, "tangentPropagation" : true, "allowEdgeOverflow" : false});
        }
        {
            var Q0;
            {var subQ0=sQuery(id+"F0.wireOp",EDGE,"E21.filletArc");var subQ1=sQuery(id+"F0.wireOp",EDGE,"E7");var subQ2=sQuery(id+"F0.wireOp",EDGE,"E6");var subQ3=sQuery(id+"F0.wireOp",EDGE,"E5");var subQ4=sQuery(id+"F0.wireOp",EDGE,"E4");var subQ5=sQuery(id+"F0.wireOp",EDGE,"E22.filletArc");var subQ6=sQuery(id+"F0.wireOp",EDGE,"E1.bottom");var subQ7=sQuery(id+"F0.wireOp",EDGE,"E1.right");var subQ8=sQuery(id+"F0.wireOp",EDGE,"E1.top");var subQ9=sQuery(id+"F0.wireOp",EDGE,"E1.left");var subQ10=sQuery(id+"F0.wireOp",EDGE,"E23.filletArc");var subQ11=sQuery(id+"F0.wireOp",EDGE,"E24.filletArc");Q0=makeQuery(id+"F2.boolean.opBoolean","SPLIT",FACE,{"disambiguationData":[TD([makeQuery(id+"F1.opExtrude","SWEPT_FACE",FACE,{"disambiguationData":[OSD([subQ6])]})])],"derivedFrom":makeQuery(id+"F1.opExtrude","CAP_FACE",FACE,{"disambiguationData":[OSD([subQ6,subQ8,subQ9,subQ7,subQ4,subQ3,subQ2,subQ1,subQ0,subQ5,subQ10,subQ11])],"isStart":true})});}
            var sketch = newSketch(context, id + "F16", { "sketchPlane" : qUnion([Q0])});
            skLineSegment(sketch, "E79", {"start": v(0, 90) * mm, "end": v(0, 120) * mm, "construction": true});
            skCircle(sketch, "E80", {"center": v(0, 120) * mm, "radius": 6 * mm});
            skLineSegment(sketch, "E81", {"start": v(-33, 90) * mm, "end": v(-15, 108) * mm});
            skLineSegment(sketch, "E82", {"start": v(-15, 108) * mm, "end": v(-15, 120) * mm});
            skArc(sketch, "E83", {"start": v(-15, 120) * mm, "mid": v(0, 135) * mm, "end": v(15, 120) * mm});
            skLineSegment(sketch, "E84", {"start": v(15, 120) * mm, "end": v(15, 108) * mm});
            skLineSegment(sketch, "E85", {"start": v(15, 108) * mm, "end": v(33, 90) * mm});
            skLineSegment(sketch, "E86", {"start": v(-80, 0) * mm, "end": v(80, 0) * mm, "construction": true});
            skLineSegment(sketch, "E87.MirrorCS", {"start": v(-33, -90) * mm, "end": v(-15, -108) * mm});
            skLineSegment(sketch, "E88.MirrorCS", {"start": v(-15, -108) * mm, "end": v(-15, -120) * mm});
            skArc(sketch, "E89.MirrorCS", {"start": v(-15, -120) * mm, "mid": v(0, -135) * mm, "end": v(15, -120) * mm});
            skLineSegment(sketch, "E90.MirrorCS", {"start": v(15, -120) * mm, "end": v(15, -108) * mm});
            skLineSegment(sketch, "E91.MirrorCS", {"start": v(15, -108) * mm, "end": v(33, -90) * mm});
            skLineSegment(sketch, "E92.MirrorCS", {"start": v(0, -90) * mm, "end": v(0, -120) * mm, "construction": true});
            skCircle(sketch, "E93.MirrorC", {"center": v(0, -120) * mm, "radius": 6 * mm});
            skSolve(sketch);
        }
        {
            var Q0;
            Q0=makeQuery(id+"F16.imprint","IMPRINT",FACE,{"disambiguationData":[TD([[makeQuery(id+"F16.imprint","IMPRINT",EDGE,{"derivedFrom":sQuery(id+"F16.wireOp",EDGE,"E80")}),-1.0]])]});
            var Q1;
            Q1=makeQuery(id+"F16.imprint","IMPRINT",FACE,{"disambiguationData":[TD([[makeQuery(id+"F16.imprint","IMPRINT",EDGE,{"derivedFrom":makeQuery(id+"F1.opExtrude","CAP_EDGE",EDGE,{"disambiguationData":[OSD([sQuery(id+"F0.wireOp",EDGE,"E1.left")])],"isStart":true})}),-1.0]])]});
            var Q2;
            {var subQ0=sQuery(id+"F16.wireOp",EDGE,"E87.MirrorCS");Q2=makeQuery(id+"F16.imprint","IMPRINT",FACE,{"disambiguationData":[TD([[makeQuery(id+"F16.imprint","IMPRINT",EDGE,{"derivedFrom":subQ0}),1.0]])]});}
            var Q3;
            Q3=makeQuery(id+"F2.opExtrude","CAP_FACE",FACE,{"disambiguationData":[OSD([sQuery(id+"F0.wireOp",EDGE,"E12"),sQuery(id+"F0.wireOp",EDGE,"E13"),sQuery(id+"F0.wireOp",EDGE,"E14"),sQuery(id+"F0.wireOp",EDGE,"E15"),sQuery(id+"F0.wireOp",EDGE,"E17.filletArc"),sQuery(id+"F0.wireOp",EDGE,"E18.filletArc"),sQuery(id+"F0.wireOp",EDGE,"E19.filletArc"),sQuery(id+"F0.wireOp",EDGE,"E20.filletArc"),sQuery(id+"F0.wireOp",EDGE,"E25.0"),sQuery(id+"F0.wireOp",EDGE,"E25.1"),sQuery(id+"F0.wireOp",EDGE,"E25.2"),sQuery(id+"F0.wireOp",EDGE,"E25.3"),sQuery(id+"F0.wireOp",EDGE,"E25.4"),sQuery(id+"F0.wireOp",EDGE,"E25.5"),sQuery(id+"F0.wireOp",EDGE,"E25.6"),sQuery(id+"F0.wireOp",EDGE,"E25.7")])],"isStart":false});
            extrude(context, id + "F17", {"entities" : qUnion([Q0, Q1, Q2]), "endBound" : BoundingType.UP_TO_SURFACE, "depth" : 25 * mm, "endBoundEntityFace" : qUnion([Q3]), "offsetDistance" : 25 * mm});
        }
    });
